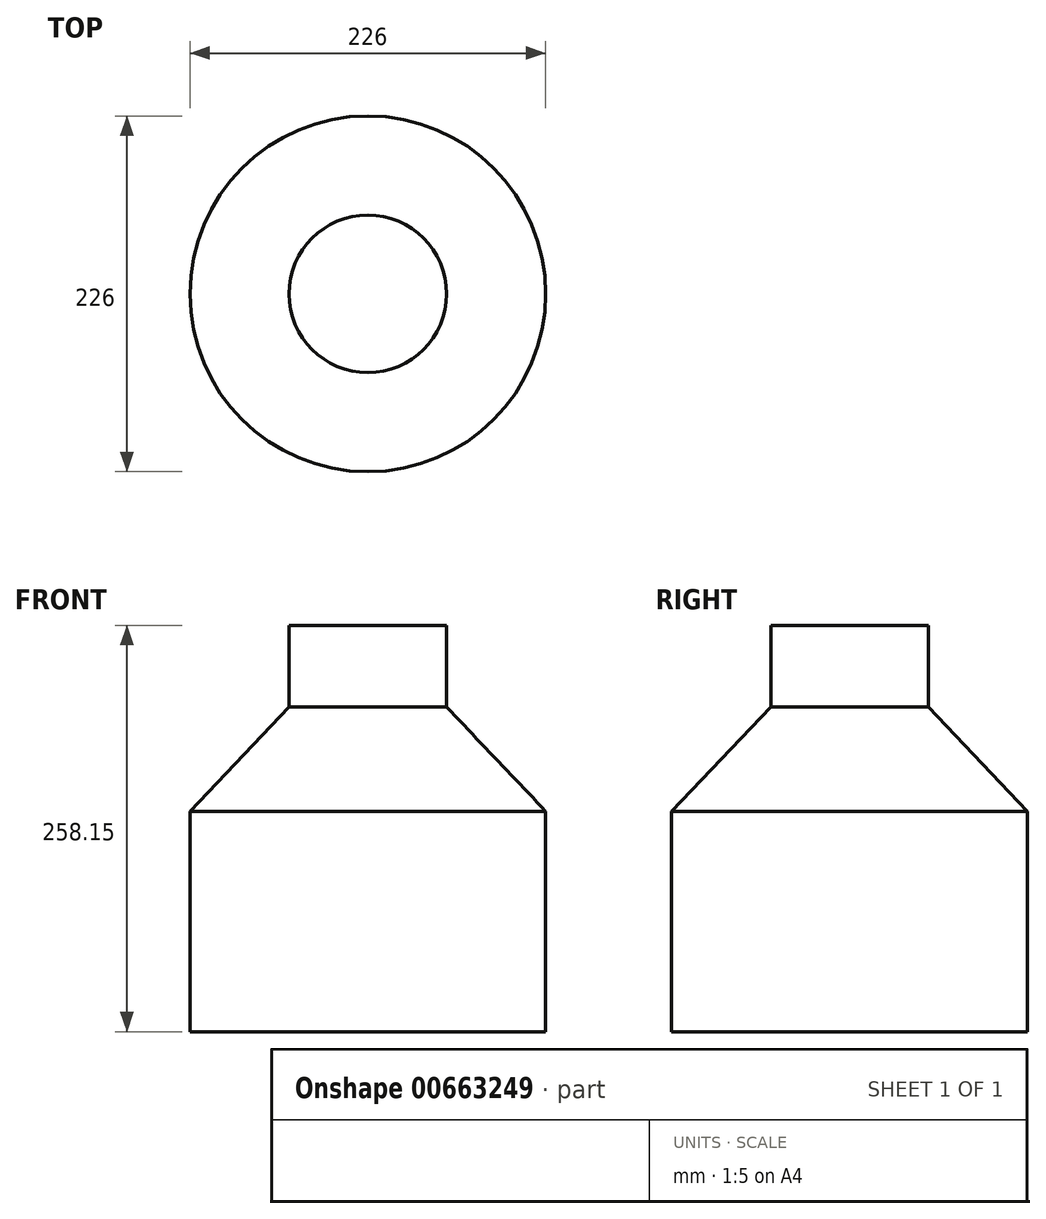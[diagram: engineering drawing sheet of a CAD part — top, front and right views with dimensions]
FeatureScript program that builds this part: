
annotation { "Feature Type Name" : "Feature", "Feature Type Description" : "" }
export const myFeature = defineFeature(function(context is Context, id is Id, definition is map)
    precondition{}
    {
        {
            var Q0;
            Q0=qCreatedBy(makeId("Front.planeOp"),FACE);
            var sketch = newSketch(context, id + "F0", { "sketchPlane" : qUnion([Q0])});
            skLineSegment(sketch, "E0", {"start": v(0, 0) * mm, "end": v(113, 0) * mm});
            skLineSegment(sketch, "E1", {"start": v(113, 0) * mm, "end": v(113, 140) * mm});
            skLineSegment(sketch, "E2", {"start": v(113, 140) * mm, "end": v(50, 206.23) * mm});
            skLineSegment(sketch, "E3", {"start": v(50, 206.23) * mm, "end": v(50, 258.15) * mm});
            skLineSegment(sketch, "E4", {"start": v(50, 258.15) * mm, "end": v(0, 258.15) * mm});
            skLineSegment(sketch, "E5", {"start": v(0, 258.15) * mm, "end": v(0, 0) * mm});
            skSolve(sketch);
        }
        {
            var Q0;
            Q0=makeQuery(id+"F0.imprint","IMPRINT",FACE,{"disambiguationData":[TD([[makeQuery(id+"F0.imprint","IMPRINT",EDGE,{"derivedFrom":sQuery(id+"F0.wireOp",EDGE,"E0")}),1.0]])]});
            var Q1;
            Q1=sQuery(id+"F0.wireOp",EDGE,"E5");
            revolve(context, id + "F1", {"surfaceOperationType" : NewSurfaceOperationType.NEW, "entities" : qUnion([Q0]), "axis" : qUnion([Q1]), "revolveType" : RevolveType.FULL});
        }
    });
